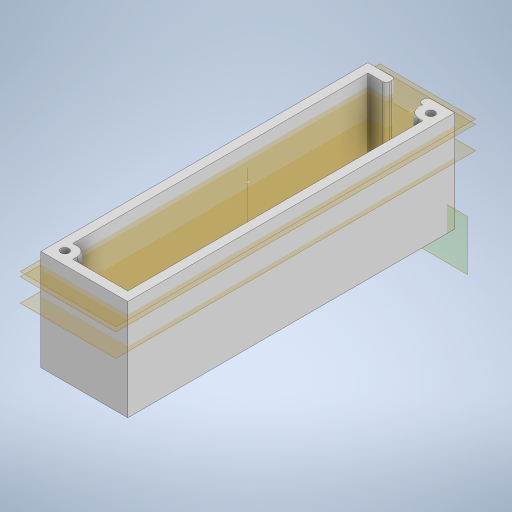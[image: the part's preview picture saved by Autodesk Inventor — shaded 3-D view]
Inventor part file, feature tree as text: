
AUTODESK INVENTOR PART (.ipt)
format: ipt  version: 2024 (Build 280153020, 153B)  size: 391,680 bytes
history: native  units: mm
features: sketch x9, extrude x6, plane x4, fillet x2, hole x1, loft x1, pattern_circular x1, projected_geometry x1, other x1
ambient origin geometry x8: Origin, YZ Plane, XZ Plane, XY Plane, X Axis, Y Axis, Z Axis, Center Point
bodies: Solid1 (feature_tree)
feature tree (26):
  sketch  "Sketch1"  dims[d0=30.0mm d1=135.0mm]
  extrude  "Extrusion1"  Depth=135.0mm
  extrude  "Extrusion2"  Depth=44.0mm TaperAngle=0.0deg
  hole  "Hole1"  [1 undecoded]
  plane  "Work Plane1"
  extrude  "Extrusion3"  Depth=14.0mm
  sketch  "Sketch4"  dims[d11=80.0mm]
  extrude  "Extrusion4"  Depth=10.25mm TaperAngle=0.0deg
  plane  "Work Plane2"
  sketch  "Sketch6"  dims[d20=50.0mm d21=10.25mm d22=0.0mm]
  plane  "Work Plane3"
  sketch  "Sketch7"  dims[d31=21.0mm d32=0.0mm d33=-7.0mm d34=-10.0mm]
  sketch  "Sketch8"  dims[d35=8.0mm d36=8.0mm]
  loft  "Loft1"
  fillet  "Fillet2"  [1 undecoded]
  plane  "Work Plane4"
  sketch  "Sketch9"  dims[d39=9.0mm d40=9.0mm d41=0.0mm d42=90.0deg d43=0.0mm d44=90.0deg d45=0.0mm d46=90.0deg d47=4.25mm d48=-5.0mm d49=5.0mm d50=2.8194mm d51=3.5mm d52=2.75mm d53=0.0mm d54=13.0mm d55=0.0mm d56=20.0mm d57=180.0deg d59=1.5mm d60=0.0mm d61=0.0mm d62=0.0mm]
  extrude  "Extrusion5"  Depth=8.0mm
  extrude  "Extrusion6"  Depth=1.5mm
  pattern_circular  "Circular Pattern1"  Angle=90.0deg  [1 undecoded]
  fillet  "Fillet3"  [1 undecoded]
  sketch  "Sketch2"  dims[d2=4.0mm d3=44.0mm d4=0.0mm]
  sketch  "Sketch3"  dims[d5=4.0mm d6=0.0mm d10=40.0mm]
  sketch  "Sketch5"  dims[d12=5.0mm d13=6.0mm d14=9.5mm d15=2.0mm d16=90.0deg d17=8.0mm d18=20.594885mm d19=14.0mm]
  projected_geometry  "Projected Loop1"
  other  "Work Axis1"
note: 4 required parameter values undecoded (feature->parameter linkage not recoverable at this tier; creation-order binding heuristic only, values carry confidence <= 0.55)
